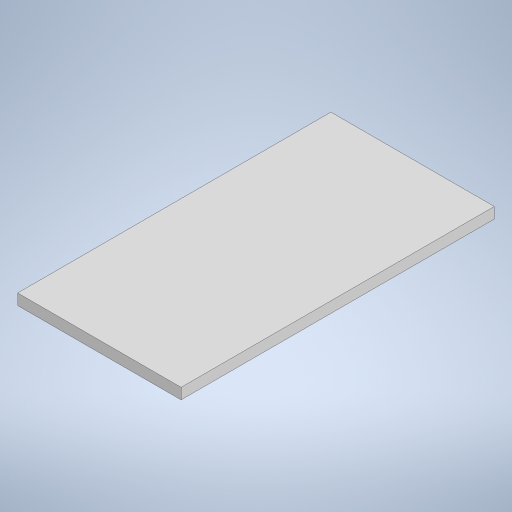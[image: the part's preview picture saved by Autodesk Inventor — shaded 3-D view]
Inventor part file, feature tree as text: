
AUTODESK INVENTOR PART (.ipt)
format: ipt  version: 2023 (Build 270158000, 158)  size: 201,728 bytes
history: native  units: mm
features: other x1, extrude x1, sketch x1
ambient origin geometry x8: Origin, YZ Plane, XZ Plane, XY Plane, X Axis, Y Axis, Z Axis, Center Point
bodies: Body1 (feature_tree)
feature tree (3):
  other  "Bryła1"
  extrude  "Wyciągnięcie proste1"  Depth=24.0mm
  sketch  "Szkic1"
